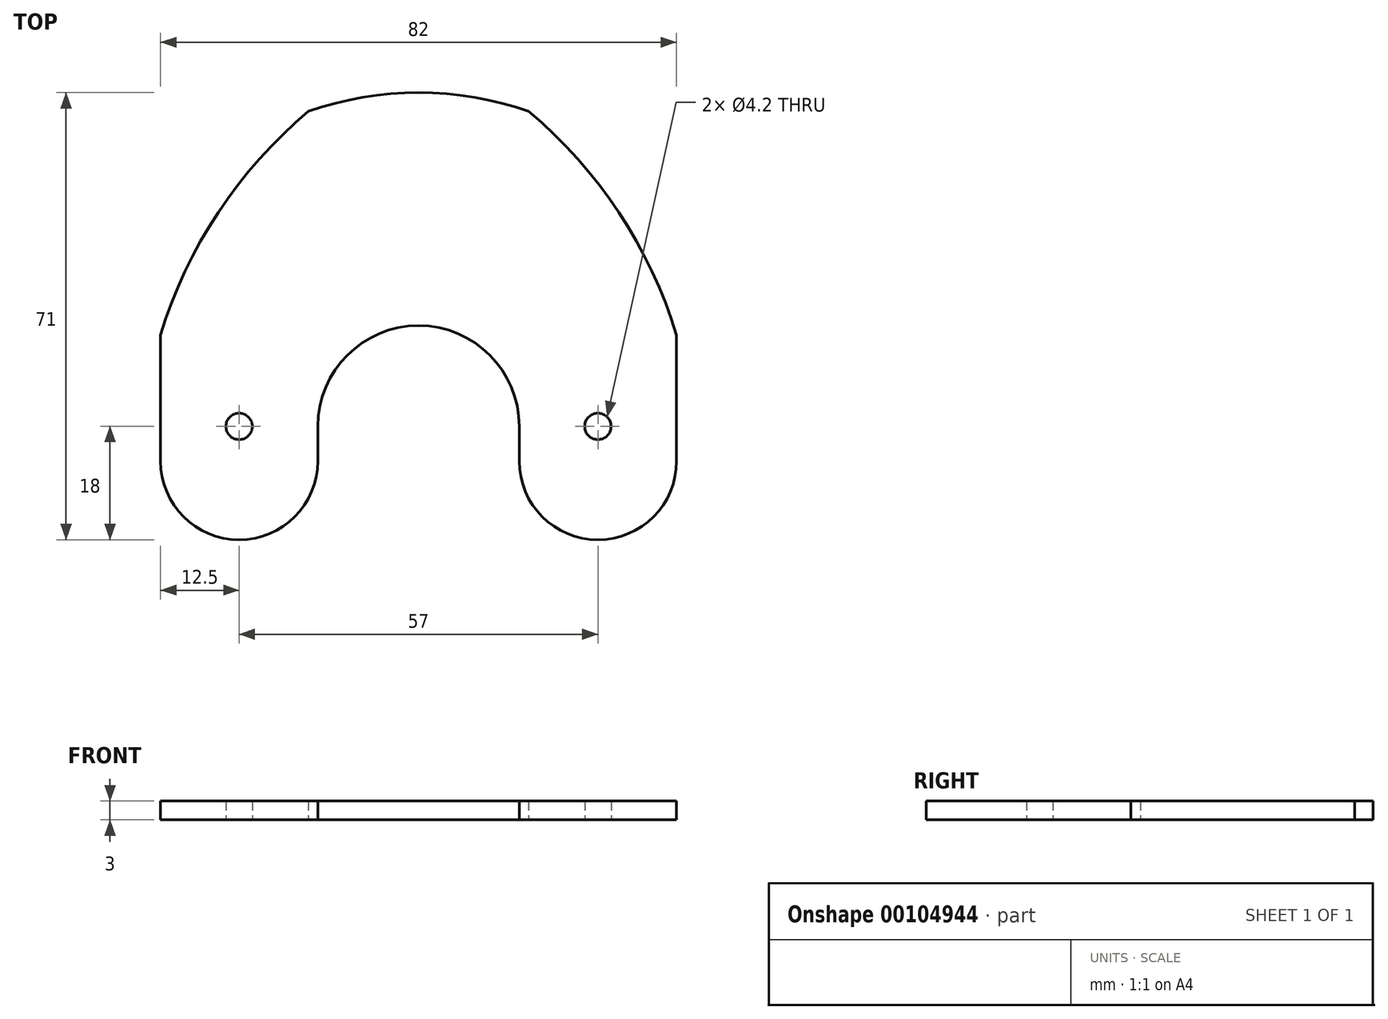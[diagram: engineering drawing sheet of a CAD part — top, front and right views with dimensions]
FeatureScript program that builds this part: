
annotation { "Feature Type Name" : "Feature", "Feature Type Description" : "" }
export const myFeature = defineFeature(function(context is Context, id is Id, definition is map)
    precondition{}
    {
        {
            var Q0;
            Q0=qCreatedBy(makeId("Top.planeOp"),FACE);
            var sketch = newSketch(context, id + "F0", { "sketchPlane" : qUnion([Q0])});
            skLineSegment(sketch, "E0", {"start": v(-41, -18) * mm, "end": v(-41, 28.1) * mm, "construction": true});
            skLineSegment(sketch, "E1", {"start": v(-41, 28.1) * mm, "end": v(-27.27, 53) * mm, "construction": true});
            skLineSegment(sketch, "E2", {"start": v(-27.27, 53) * mm, "end": v(27.27, 53) * mm, "construction": true});
            skLineSegment(sketch, "E3", {"start": v(27.27, 53) * mm, "end": v(41, 28.1) * mm, "construction": true});
            skLineSegment(sketch, "E4", {"start": v(41, 28.1) * mm, "end": v(41, -18) * mm, "construction": true});
            skLineSegment(sketch, "E5", {"start": v(41, -18) * mm, "end": v(16, -18) * mm, "construction": true});
            skLineSegment(sketch, "E6", {"start": v(16, -18) * mm, "end": v(16, 16) * mm, "construction": true});
            skLineSegment(sketch, "E7", {"start": v(16, 16) * mm, "end": v(-16, 16) * mm, "construction": true});
            skLineSegment(sketch, "E8", {"start": v(-16, 16) * mm, "end": v(-16, -18) * mm, "construction": true});
            skLineSegment(sketch, "E9", {"start": v(-16, -18) * mm, "end": v(-41, -18) * mm, "construction": true});
            skCircle(sketch, "E10", {"center": v(0, 0) * mm, "radius": 16 * mm, "construction": true});
            skCircle(sketch, "E11", {"center": v(-28.5, 0) * mm, "radius": 2.1 * mm});
            skCircle(sketch, "E12", {"center": v(28.5, 0) * mm, "radius": 2.1 * mm});
            skArc(sketch, "E13", {"start": v(-41, -5.5) * mm, "mid": v(-28.5, -18) * mm, "end": v(-16, -5.5) * mm});
            skArc(sketch, "E14", {"start": v(16, -5.5) * mm, "mid": v(28.5, -18) * mm, "end": v(41, -5.5) * mm});
            skArc(sketch, "E15", {"start": v(17.5, 50.03) * mm, "mid": v(0, 53) * mm, "end": v(-17.5, 50.03) * mm});
            skArc(sketch, "E16", {"start": v(-17.5, 50.03) * mm, "mid": v(-31.83, 33.97) * mm, "end": v(-41, 14.5) * mm});
            skArc(sketch, "E17", {"start": v(41, 14.5) * mm, "mid": v(31.83, 33.97) * mm, "end": v(17.5, 50.03) * mm});
            skLineSegment(sketch, "E18", {"start": v(-41, -5.5) * mm, "end": v(-41, 14.5) * mm});
            skLineSegment(sketch, "E19", {"start": v(-16, -5.5) * mm, "end": v(-16, 0) * mm});
            skArc(sketch, "E20", {"start": v(16, 0) * mm, "mid": v(0, 16) * mm, "end": v(-16, 0) * mm});
            skLineSegment(sketch, "E21", {"start": v(16, 0) * mm, "end": v(16, -5.5) * mm});
            skLineSegment(sketch, "E22", {"start": v(41, -5.5) * mm, "end": v(41, 14.5) * mm});
            skSolve(sketch);
        }
        {
            var Q0;
            Q0 = qSketchRegion(id + "F0", true);
            extrude(context, id + "F1", {"entities" : qUnion([Q0]), "depth" : 3 * mm});
        }
    });
